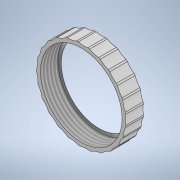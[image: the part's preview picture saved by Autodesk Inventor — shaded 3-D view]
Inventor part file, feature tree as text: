
AUTODESK INVENTOR PART (.ipt)
format: ipt  version: 2020.2 (Build 242310000, 310)  size: 725,504 bytes
history: native  units: mm
features: other x3, plane x1, split x1, sketch x1
ambient origin geometry x8: Origin, YZ Plane, XZ Plane, XY Plane, X Axis, Y Axis, Z Axis, Center Point
bodies: Solid1 (feature_tree), Solid2 (feature_tree), Solid3 (feature_tree)
feature tree (6):
  other  "Part5.ipt"
  plane  "Work Plane1"
  split  "Split1"
  other  "Solid3::Part5.ipt"
  other  "TaggingFeature1"
  sketch  "Sketch1"  dims[d0=10.0mm d1=-22.5mm d2=0.85mm]
